# Revit family: Haworth_Contour_Light
name_source: partatom
category: Lighting Fixtures
revit_build: Autodesk Revit 2018 (Build: 20170223_1515(x64)
units: mm (PartAtom-declared; Revit-internal decimal feet)

## family parameters
Always vertical = Yes
Cut with Voids When Loaded = No
Light Source = Yes
OmniClass Number = 23.80.70.11.14
OmniClass Title = General Luminaries, Directional
Part Type = Normal
Room Calculation Point = No
Round Connector Dimension = Use Diameter
Shared = No
Work Plane-Based = No

## types (3) — shared parameters
Assembly Code = D5020200
Base Finish = Haworth _ Paint _ Collection White
Base Radius = 1 1/2"
Color Filter = 16777215
Dimming Lamp Color Temperature Shift = <None>
Emit Shape Visible in Rendering = No
Emit from Circle Diameter = 12"
Glass Finish = Haworth _ Glass _ Clear
Inside Lamp Radius = 3 47/256"
Interior Finish = Haworth _ Wood _ Walnut
Lamp Thickness Offset = 1/4"
Manufacturer = Haworth
Outside Lamp Radius = 3 111/256"
Photometric Web File = generic
Revision Number = 1
Size = Verify Final Dim. w/ Haworth
Tilt Angle = 90.00°
URL = http://www.haworth.com
URL - Product = https://www.haworth.com
Warranty = http://www.haworth.com
Wattage Comments = 8-21.5W 120V 60Hz

## per-type parameters (varying)
| type | Actual Depth | Actual Height | Actual Width | Description | Floor Lamp | Large Table Lamp | Model | Small Table Lamp |
| LCF1-6009 - Floor Light | 8" | 60" | 13" | Haworth Contour Floor Light | Yes | No | LCF1-6009 | No |
| LCT1-1708 - Small Table Light | 6" | 17 1/2" | 12" | Haworth Contour Table Light Small | No | No | LCT1-1708 | Yes |
| LCT1-2508 - Large Table Light | 6" | 25" | 13" | Haworth Contour Table Light Large | No | Yes | LCT1-2508 | No |

## geometry (parser evidence)
native form markers: Sweep x2
no freeform markers — native parametric forms only
